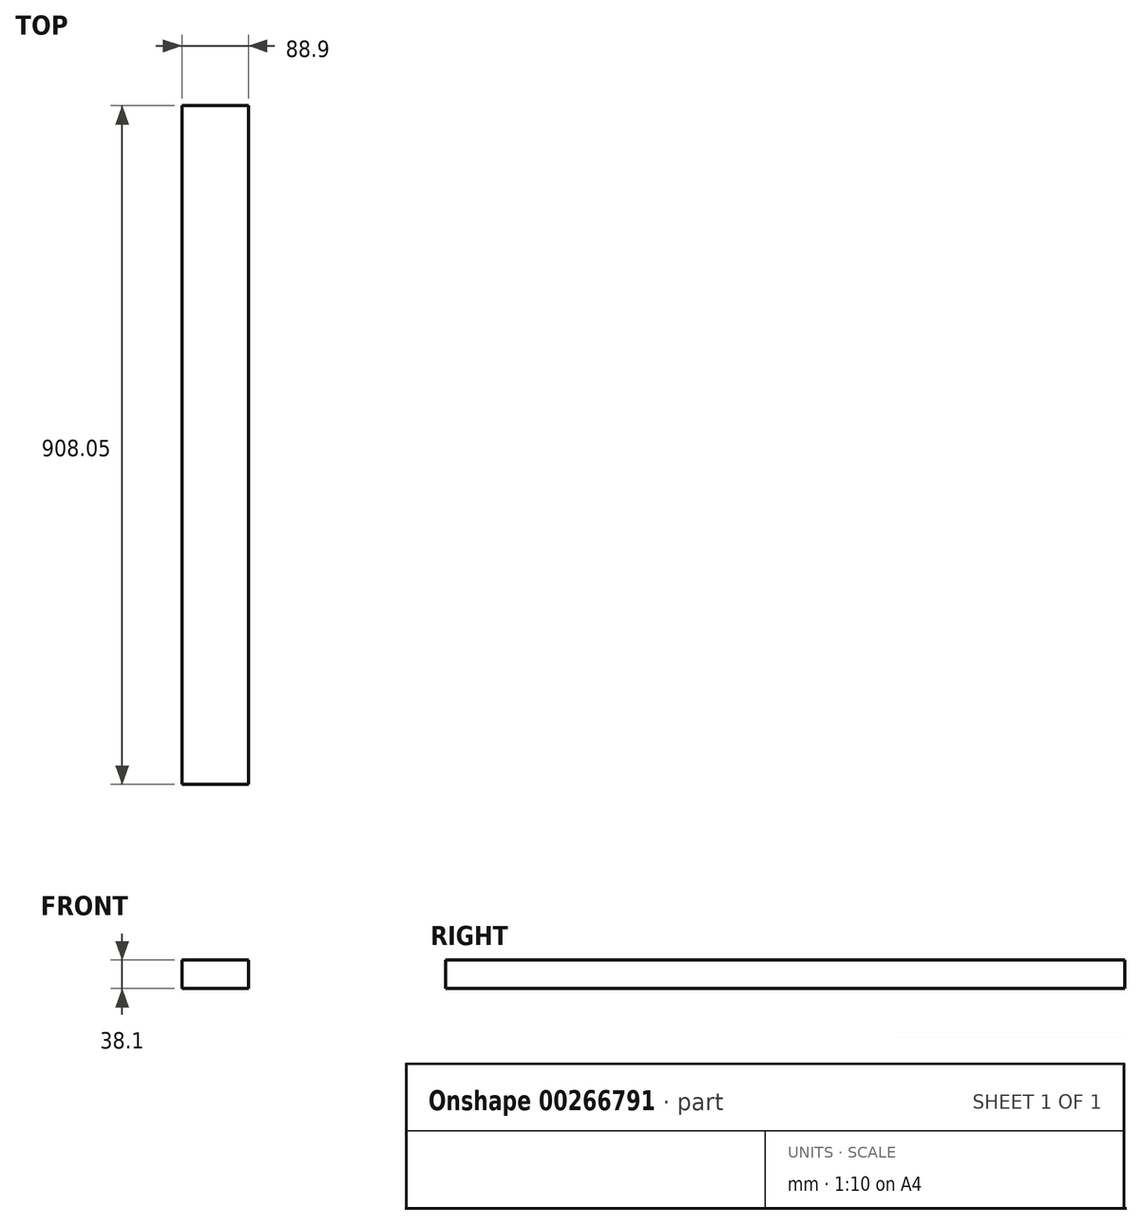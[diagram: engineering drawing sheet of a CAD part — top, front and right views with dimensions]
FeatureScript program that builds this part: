
annotation { "Feature Type Name" : "Feature", "Feature Type Description" : "" }
export const myFeature = defineFeature(function(context is Context, id is Id, definition is map)
    precondition{}
    {
        {
            var Q0;
            Q0=qCreatedBy(makeId("Front.planeOp"),FACE);
            var sketch = newSketch(context, id + "F0", { "sketchPlane" : qUnion([Q0])});
            skLineSegment(sketch, "E0.bottom", {"start": v(-48.34, 23.68) * mm, "end": v(40.56, 23.68) * mm});
            skLineSegment(sketch, "E0.top", {"start": v(-48.34, -14.42) * mm, "end": v(40.56, -14.42) * mm});
            skLineSegment(sketch, "E0.left", {"start": v(-48.34, 23.68) * mm, "end": v(-48.34, -14.42) * mm});
            skLineSegment(sketch, "E0.right", {"start": v(40.56, 23.68) * mm, "end": v(40.56, -14.42) * mm});
            skSolve(sketch);
        }
        {
            var Q0;
            Q0=qSketchRegion(id+"F0",true);
            extrude(context, id + "F1", {"entities" : qUnion([Q0]), "depth" : 908.05 * mm});
        }
    });
